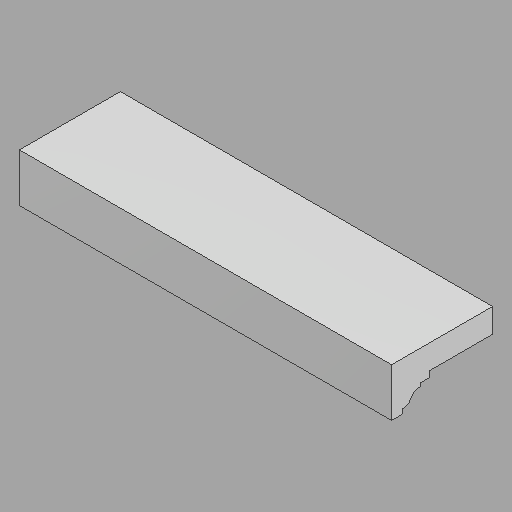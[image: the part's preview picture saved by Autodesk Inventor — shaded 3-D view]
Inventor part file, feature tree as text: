
AUTODESK INVENTOR PART (.ipt)
format: ipt  version: 2023 (Build 270158000, 158)  size: 131,072 bytes
history: native  units: in
note: dims shown in document units (in); Inventor stores cm internally (conversion verified against a paired STEP export)
features: plane x1, extrude x1, sketch x1, projected_geometry x1, other x1
ambient origin geometry x8: Origin, YZ Plane, XZ Plane, XY Plane, X Axis, Y Axis, Z Axis, Center Point
bodies: Solid1 (feature_tree)
feature tree (5):
  plane  "Work Plane1"
  extrude  "Extrusion1"  Depth=71.125in TaperAngle=0.0deg
  sketch  "Sketch1"  dims[d0=-30.875in d1=71.125in d2=0.0in]
  projected_geometry  "Projected Loop1"
  other  "Ornate (1)"
